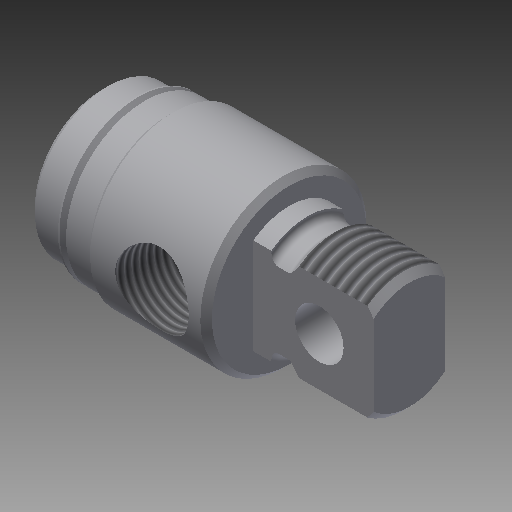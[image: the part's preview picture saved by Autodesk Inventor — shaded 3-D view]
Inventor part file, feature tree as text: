
AUTODESK INVENTOR PART (.ipt)
format: ipt  version: 2019.4 (Build 234330000, 330)  size: 349,184 bytes
history: native  units: in
note: dims shown in document units (in); Inventor stores cm internally (conversion verified against a paired STEP export)
features: other x154, sketch x7, revolve x4, thread x2, extrude x2, hole x1
ambient origin geometry x8: Origin, YZ Plane, XZ Plane, XY Plane, X Axis, Y Axis, Z Axis, Center Point
bodies: Solid1 (feature_tree)
feature tree (170):
  revolve  "Revolution1"  Angle=360.0deg
  revolve  "Revolution2"  [1 undecoded]
  thread  "Thread1"  [1 undecoded]
  extrude  "Extrusion1"  TaperAngle=360.0deg  [1 undecoded]
  hole  "Hole1"  [1 undecoded]
  revolve  "Revolution3"  [1 undecoded]
  thread  "Thread2"  [1 undecoded]
  revolve  "Revolution4"  [1 undecoded]
  extrude  "Extrusion2"  [1 undecoded]
  other  "1_XY"
  other  "1_YZ"
  other  "1_ZX"
  other  "1_X"
  other  "1_Y"
  other  "1_Z"
  other  "1_Center"
  other  "c1_XY"
  other  "c1_YZ"
  other  "c1_ZX"
  other  "c1_X"
  other  "c1_Y"
  other  "c1_Z"
  other  "c1_Center"
  other  "c2_XY"
  other  "c2_YZ"
  other  "c2_ZX"
  other  "c2_X"
  other  "c2_Y"
  other  "c2_Z"
  other  "c2_Center"
  other  "cc1_XY"
  other  "cc1_YZ"
  other  "cc1_ZX"
  other  "cc1_X"
  other  "cc1_Y"
  other  "cc1_Z"
  other  "cc1_Center"
  other  "cc2_XY"
  other  "cc2_YZ"
  other  "cc2_ZX"
  other  "cc2_X"
  other  "cc2_Y"
  other  "cc2_Z"
  other  "cc2_Center"
  other  "lovra1_XY"
  other  "lovra1_YZ"
  other  "lovra1_ZX"
  other  "lovra1_X"
  other  "lovra1_Y"
  other  "lovra1_Z"
  other  "lovra1_Center"
  other  "lovra2_XY"
  other  "lovra2_YZ"
  other  "lovra2_ZX"
  other  "lovra2_X"
  other  "lovra2_Y"
  other  "lovra2_Z"
  other  "lovra2_Center"
  other  "lovra21_XY"
  other  "lovra21_YZ"
  other  "lovra21_ZX"
  other  "lovra21_X"
  other  "lovra21_Y"
  other  "lovra21_Z"
  other  "lovra21_Center"
  other  "lovra22_XY"
  other  "lovra22_YZ"
  other  "lovra22_ZX"
  other  "lovra22_X"
  other  "lovra22_Y"
  other  "lovra22_Z"
  other  "lovra22_Center"
  other  "lovra3_XY"
  other  "lovra3_YZ"
  other  "lovra3_ZX"
  other  "lovra3_X"
  other  "lovra3_Y"
  other  "lovra3_Z"
  other  "lovra3_Center"
  other  "olen_XY"
  other  "olen_YZ"
  other  "olen_ZX"
  other  "olen_X"
  other  "olen_Y"
  other  "olen_Z"
  other  "olen_Center"
  other  "p1_XY"
  other  "p1_YZ"
  other  "p1_ZX"
  other  "p1_X"
  other  "p1_Y"
  other  "p1_Z"
  other  "p1_Center"
  other  "p2_XY"
  other  "p2_YZ"
  other  "p2_ZX"
  other  "p2_X"
  other  "p2_Y"
  other  "p2_Z"
  other  "p2_Center"
  other  "port_XY"
  other  "port_YZ"
  other  "port_ZX"
  other  "port_X"
  other  "port_Y"
  other  "port_Z"
  other  "port_Center"
  other  "port2_XY"
  other  "port2_YZ"
  other  "port2_ZX"
  other  "port2_X"
  other  "port2_Y"
  other  "port2_Z"
  other  "port2_Center"
  other  "thd1_XY"
  other  "thd1_YZ"
  other  "thd1_ZX"
  other  "thd1_X"
  other  "thd1_Y"
  other  "thd1_Z"
  other  "thd1_Center"
  other  "thd2_XY"
  other  "thd2_YZ"
  other  "thd2_ZX"
  other  "thd2_X"
  other  "thd2_Y"
  other  "thd2_Z"
  other  "thd2_Center"
  other  "to_mounting_bracket_XY"
  other  "to_mounting_bracket_YZ"
  other  "to_mounting_bracket_ZX"
  other  "to_mounting_bracket_X"
  other  "to_mounting_bracket_Y"
  other  "to_mounting_bracket_Z"
  other  "to_mounting_bracket_Center"
  other  "to_nut_XY"
  other  "to_nut_YZ"
  other  "to_nut_ZX"
  other  "to_nut_X"
  other  "to_nut_Y"
  other  "to_nut_Z"
  other  "to_nut_Center"
  other  "to_pin_XY"
  other  "to_pin_YZ"
  other  "to_pin_ZX"
  other  "to_pin_X"
  other  "to_pin_Y"
  other  "to_pin_Z"
  other  "to_pin_Center"
  other  "to_screw_XY"
  other  "to_screw_YZ"
  other  "to_screw_ZX"
  other  "to_screw_X"
  other  "to_screw_Y"
  other  "to_screw_Z"
  other  "to_screw_Center"
  other  "to_tube_XY"
  other  "to_tube_YZ"
  other  "to_tube_ZX"
  other  "to_tube_X"
  other  "to_tube_Y"
  other  "to_tube_Z"
  other  "to_tube_Center"
  sketch  "Sketch_8"  dims[d2=0.3547in d3=0.0in d4=0.625in d5=0.0in]
  sketch  "Sketch_15"  dims[d14=0.3021in d15=0.0in d16=360.0deg]
  sketch  "Sketch_9"  dims[d6=0.312in d7=0.75in d8=0.375in d9=0.25in d10=0.5635in d11=0.9284in d12=120.0deg d13=360.0deg]
  sketch  "Sketch4"  dims[d0=360.0deg d1=360.0deg]
  sketch  "Sketch_68"
  sketch  "Sketch_24"  dims[d17=0.5587in d18=0.0in]
  sketch  "Sketch_43"  dims[d19=0.0in d20=0.0in d21=0.0in d22=0.0in d23=0.0in d24=0.0in d25=0.0in d26=0.0in]
note: 8 required parameter values undecoded (feature->parameter linkage not recoverable at this tier; creation-order binding heuristic only, values carry confidence <= 0.55)